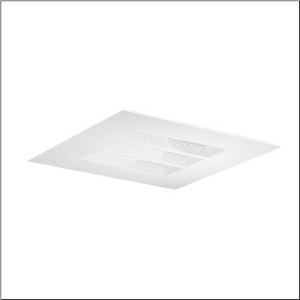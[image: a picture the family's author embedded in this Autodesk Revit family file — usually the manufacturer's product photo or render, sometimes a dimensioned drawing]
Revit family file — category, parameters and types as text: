
# Revit family: taris_r__21_51mt1ld0jhgddc02_9e63
name_source: partatom
category: Lighting Fixtures
units: mm (PartAtom-declared; Revit-internal decimal feet)

## family parameters
Cut with Voids When Loaded = No
Host = Face
Light Source = No
Part Type = Normal
Room Calculation Point = No
Round Connector Dimension = Use Diameter
Shared = No

## types (1)
- --- (1 x LED, 4620 lm, 27.4 W, 4000K)
    Apparent Load = 27 VA
    CIE Flux Codes = 79 97 100 100 100
    Color Rendering = 80
    Color Temperature = 4000K
    Default Elevation = 1800 mm
    Description = Taris® 21, office luminaire, primary anti-glare with micro louvre, primary optical cover: axial lens, of PMMA, structured, CAT 2 (L<= 1500cd/m²), light emission: direct distribution, primary light characteristic: symmetric, installation type: lay-in mounting, LED rated luminous flux: 4.620 lm, light colour: 840, colour temperature: 4000K, control gear: ECG DALI, with terminal, 5-pole, mains connection: 230V, AC, 50Hz, rated input power: 27W, housing, luminaire housing, of plastic, traffic white (RAL 9016), module: M625, length: 622 mm, width: 622 mm, height: 42mm, protection rating (complete): IP20, insulation class (complete): insulation class I (protective earthing), certification: CE, ENEC, VDE, protection symbol: F, impact resistance: IK02, permissible ambient temperature for indoor applications: 0..+35°C, standard: EN 50419, packaging unit: 1 piece
    Height = 0 mm  [stored 0 ft]
    Lamp = 1 x LED
    Lamp Light Flux = 4620 lm
    Lamp Power = 27.4 W
    Lamp count = 1
    Length = 622 mm
    Luminous efficacy = 169 lm/W
    Manufacturer = Siteco
    ModVariant = No
    Model = 51MT1LD0JHGDDC02
    Mounting Place = Ceiling
    Mounting Type = Recessed
    Number of Poles = 1
    OnlyDefault = Yes
    Power Factor = 1
    Product Name = Taris® 21
    Product group = office luminaire | ceiling recessed
    ProductGroupID = 400
    Protection Class = Protection class I
    Protection Degree = IP 20
    RLX_Detail_Level = 1
    RlxData = <blob elided: 23337 chars, md5=57fe206e>
    Socket = socket
    Standby Power = 0 W
    System Light Flux = 4620 lm
    System Power = 27 W
    Type Comments = factory setting: luminous flux: 100 % | dim-lin: 254 | 250 mA
    Type Image = l_1004820.jpg
    URL = http://relux.com
    VarID = @adj_130535
    Voltage = 0 V
    Weight = 0.00 kg
    Width = 622 mm

note: [stored X ft] marks values corroborated as IEEE doubles in the binary element streams (Revit-internal decimal feet)

## geometry (parser evidence)
native form markers: Blend x4, Sweep x10
no freeform markers — native parametric forms only
